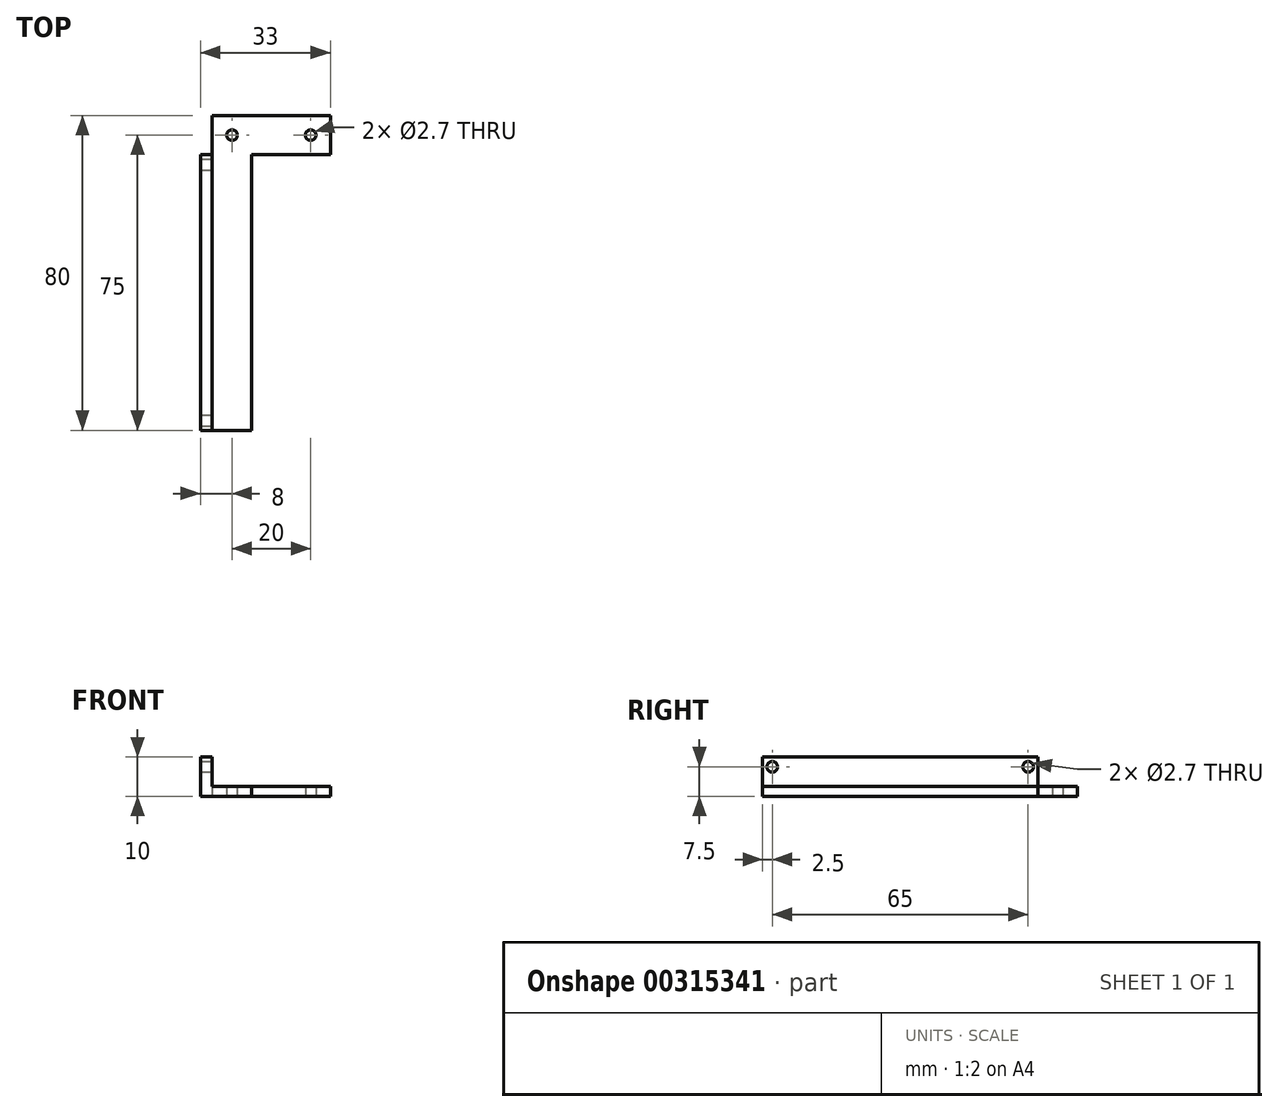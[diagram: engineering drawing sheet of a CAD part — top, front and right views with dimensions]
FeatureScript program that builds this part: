
annotation { "Feature Type Name" : "Feature", "Feature Type Description" : "" }
export const myFeature = defineFeature(function(context is Context, id is Id, definition is map)
    precondition{}
    {
        {
            var Q0;
            Q0=qCreatedBy(makeId("Top.planeOp"),FACE);
            var sketch = newSketch(context, id + "F0", { "sketchPlane" : qUnion([Q0])});
            skLineSegment(sketch, "E0", {"start": v(19.59, 71.65) * mm, "end": v(-10.41, 71.65) * mm});
            skLineSegment(sketch, "E1", {"start": v(-10.41, 71.65) * mm, "end": v(-10.41, -8.35) * mm});
            skLineSegment(sketch, "E2", {"start": v(-10.41, -8.35) * mm, "end": v(-0.41, -8.35) * mm});
            skLineSegment(sketch, "E3", {"start": v(-0.41, -8.35) * mm, "end": v(-0.41, 61.65) * mm});
            skLineSegment(sketch, "E4", {"start": v(-0.41, 61.65) * mm, "end": v(19.59, 61.65) * mm});
            skLineSegment(sketch, "E5", {"start": v(19.59, 61.65) * mm, "end": v(19.59, 71.65) * mm});
            skLineSegment(sketch, "E6", {"start": v(-10.41, 61.65) * mm, "end": v(-13.41, 61.65) * mm});
            skLineSegment(sketch, "E7", {"start": v(-13.41, 61.65) * mm, "end": v(-13.41, -8.35) * mm});
            skLineSegment(sketch, "E8", {"start": v(-13.41, -8.35) * mm, "end": v(-10.41, -8.35) * mm});
            skLineSegment(sketch, "E9", {"start": v(-10.41, 66.65) * mm, "end": v(19.59, 66.65) * mm, "construction": true});
            skCircle(sketch, "E10", {"center": v(-5.41, 66.65) * mm, "radius": 1.35 * mm});
            skCircle(sketch, "E11", {"center": v(14.59, 66.65) * mm, "radius": 1.35 * mm});
            skSolve(sketch);
        }
        {
            var Q0;
            Q0=makeQuery(id+"F0.imprint","IMPRINT",FACE,{"disambiguationData":[TD([[makeQuery(id+"F0.imprint","IMPRINT",EDGE,{"derivedFrom":sQuery(id+"F0.wireOp",EDGE,"E0")}),1.0]])]});
            extrude(context, id + "F1", {"entities" : qUnion([Q0]), "depth" : 2.5 * mm});
        }
        {
            var Q0;
            Q0=makeQuery(id+"F0.imprint","IMPRINT",FACE,{"disambiguationData":[TD([[makeQuery(id+"F0.imprint","IMPRINT",EDGE,{"derivedFrom":sQuery(id+"F0.wireOp",EDGE,"E1")}),-1.0]])]});
            extrude(context, id + "F2", {"entities" : qUnion([Q0]), "operationType" : NewBodyOperationType.ADD, "depth" : 10 * mm});
        }
        {
            var Q0;
            Q0=makeQuery(id+"F2.opExtrude","SWEPT_FACE",FACE,{"disambiguationData":[OSD([sQuery(id+"F0.wireOp",EDGE,"E1")])]});
            var sketch = newSketch(context, id + "F3", { "sketchPlane" : qUnion([Q0])});
            skLineSegment(sketch, "E12", {"start": v(-8.35, 7.5) * mm, "end": v(61.65, 7.5) * mm, "construction": true});
            skCircle(sketch, "E13", {"center": v(-5.85, 7.5) * mm, "radius": 1.35 * mm});
            skCircle(sketch, "E14", {"center": v(59.15, 7.5) * mm, "radius": 1.35 * mm});
            skSolve(sketch);
        }
        {
            var Q0;
            Q0=makeQuery(id+"F3.imprint","IMPRINT",FACE,{"disambiguationData":[TD([[makeQuery(id+"F3.imprint","IMPRINT",EDGE,{"derivedFrom":sQuery(id+"F3.wireOp",EDGE,"E13")}),1.0]])]});
            var Q1;
            Q1=makeQuery(id+"F3.imprint","IMPRINT",FACE,{"disambiguationData":[TD([[makeQuery(id+"F3.imprint","IMPRINT",EDGE,{"derivedFrom":sQuery(id+"F3.wireOp",EDGE,"E14")}),1.0]])]});
            extrude(context, id + "F4", {"entities" : qUnion([Q0, Q1]), "operationType" : NewBodyOperationType.REMOVE, "endBound" : BoundingType.THROUGH_ALL, "oppositeDirection" : true, "depth" : 25 * mm});
        }
    });
